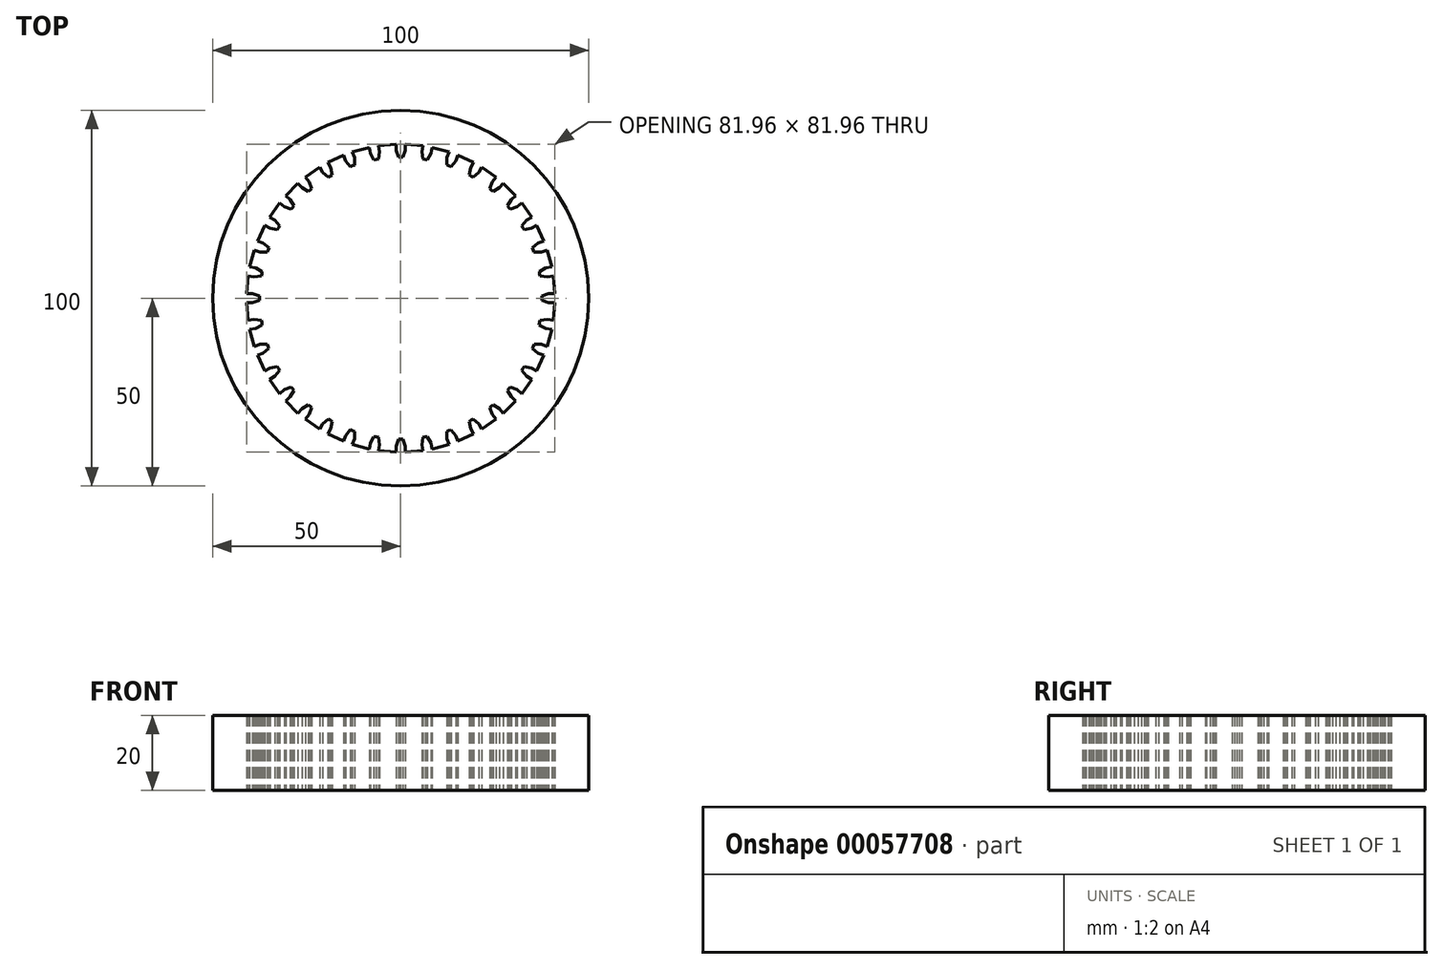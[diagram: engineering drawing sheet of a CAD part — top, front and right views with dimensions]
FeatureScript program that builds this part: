
annotation { "Feature Type Name" : "Feature", "Feature Type Description" : "" }
export const myFeature = defineFeature(function(context is Context, id is Id, definition is map)
    precondition{}
    {
        {
            var Q0;
            Q0=qCreatedBy(makeId("Top.planeOp"),FACE);
            var sketch = newSketch(context, id + "F0", { "sketchPlane" : qUnion([Q0])});
            skCircle(sketch, "E0", {"center": v(0, 0) * mm, "radius": 50 * mm});
            skLineSegment(sketch, "E1", {"start": v(0, 41) * mm, "end": v(0, 37.5) * mm});
            skLineSegment(sketch, "E2.0", {"start": v(-1.25, 40.98) * mm, "end": v(-1.25, 37.78) * mm});
            skLineSegment(sketch, "E3.0", {"start": v(1.25, 40.98) * mm, "end": v(1.25, 37.78) * mm});
            skPoint(sketch, "E4.visualSharp", {"position": v(1.25, 37.48) * mm});
            skPoint(sketch, "E5.visualSharp", {"position": v(-1.25, 37.48) * mm});
            skLineSegment(sketch, "E6.1.0", {"start": v(-8.35, 40.14) * mm, "end": v(-7.8, 36.99) * mm});
            skArc(sketch, "E6.1.1", {"start": v(-7.8, 36.99) * mm, "mid": v(-7.67, 36.8) * mm, "end": v(-7.44, 36.74) * mm});
            skLineSegment(sketch, "E6.1.2", {"start": v(-7.44, 36.74) * mm, "end": v(-5.57, 37.07) * mm});
            skArc(sketch, "E6.1.3", {"start": v(-5.57, 37.07) * mm, "mid": v(-5.38, 37.2) * mm, "end": v(-5.33, 37.42) * mm});
            skLineSegment(sketch, "E6.1.4", {"start": v(-5.89, 40.58) * mm, "end": v(-5.33, 37.42) * mm});
            skLineSegment(sketch, "E6.2.0", {"start": v(-15.2, 38.08) * mm, "end": v(-14.1, 35.07) * mm});
            skArc(sketch, "E6.2.1", {"start": v(-14.1, 35.07) * mm, "mid": v(-13.94, 34.9) * mm, "end": v(-13.71, 34.9) * mm});
            skLineSegment(sketch, "E6.2.2", {"start": v(-13.71, 34.9) * mm, "end": v(-11.93, 35.54) * mm});
            skArc(sketch, "E6.2.3", {"start": v(-11.93, 35.54) * mm, "mid": v(-11.76, 35.7) * mm, "end": v(-11.75, 35.93) * mm});
            skLineSegment(sketch, "E6.2.4", {"start": v(-12.84, 38.94) * mm, "end": v(-11.75, 35.93) * mm});
            skLineSegment(sketch, "E6.3.0", {"start": v(-21.57, 34.87) * mm, "end": v(-19.97, 32.1) * mm});
            skArc(sketch, "E6.3.1", {"start": v(-19.97, 32.1) * mm, "mid": v(-19.79, 31.95) * mm, "end": v(-19.56, 31.98) * mm});
            skLineSegment(sketch, "E6.3.2", {"start": v(-19.56, 31.98) * mm, "end": v(-17.92, 32.93) * mm});
            skArc(sketch, "E6.3.3", {"start": v(-17.92, 32.93) * mm, "mid": v(-17.78, 33.12) * mm, "end": v(-17.8, 33.34) * mm});
            skLineSegment(sketch, "E6.3.4", {"start": v(-19.4, 36.12) * mm, "end": v(-17.8, 33.34) * mm});
            skLineSegment(sketch, "E6.4.0", {"start": v(-27.3, 30.59) * mm, "end": v(-25.24, 28.14) * mm});
            skArc(sketch, "E6.4.1", {"start": v(-25.24, 28.14) * mm, "mid": v(-25.04, 28.03) * mm, "end": v(-24.82, 28.1) * mm});
            skLineSegment(sketch, "E6.4.2", {"start": v(-24.82, 28.1) * mm, "end": v(-23.36, 29.32) * mm});
            skArc(sketch, "E6.4.3", {"start": v(-23.36, 29.32) * mm, "mid": v(-23.26, 29.53) * mm, "end": v(-23.33, 29.74) * mm});
            skLineSegment(sketch, "E6.4.4", {"start": v(-25.38, 32.2) * mm, "end": v(-23.33, 29.74) * mm});
            skLineSegment(sketch, "E6.5.0", {"start": v(-32.2, 25.38) * mm, "end": v(-29.74, 23.33) * mm});
            skArc(sketch, "E6.5.1", {"start": v(-29.74, 23.33) * mm, "mid": v(-29.53, 23.26) * mm, "end": v(-29.32, 23.36) * mm});
            skLineSegment(sketch, "E6.5.2", {"start": v(-29.32, 23.36) * mm, "end": v(-28.1, 24.82) * mm});
            skArc(sketch, "E6.5.3", {"start": v(-28.1, 24.82) * mm, "mid": v(-28.03, 25.04) * mm, "end": v(-28.14, 25.24) * mm});
            skLineSegment(sketch, "E6.5.4", {"start": v(-30.59, 27.3) * mm, "end": v(-28.14, 25.24) * mm});
            skLineSegment(sketch, "E6.6.0", {"start": v(-36.12, 19.4) * mm, "end": v(-33.34, 17.8) * mm});
            skArc(sketch, "E6.6.1", {"start": v(-33.34, 17.8) * mm, "mid": v(-33.12, 17.78) * mm, "end": v(-32.93, 17.92) * mm});
            skLineSegment(sketch, "E6.6.2", {"start": v(-32.93, 17.92) * mm, "end": v(-31.98, 19.56) * mm});
            skArc(sketch, "E6.6.3", {"start": v(-31.98, 19.56) * mm, "mid": v(-31.95, 19.79) * mm, "end": v(-32.1, 19.97) * mm});
            skLineSegment(sketch, "E6.6.4", {"start": v(-34.87, 21.57) * mm, "end": v(-32.1, 19.97) * mm});
            skLineSegment(sketch, "E6.7.0", {"start": v(-38.94, 12.84) * mm, "end": v(-35.93, 11.75) * mm});
            skArc(sketch, "E6.7.1", {"start": v(-35.93, 11.75) * mm, "mid": v(-35.7, 11.76) * mm, "end": v(-35.54, 11.93) * mm});
            skLineSegment(sketch, "E6.7.2", {"start": v(-35.54, 11.93) * mm, "end": v(-34.9, 13.71) * mm});
            skArc(sketch, "E6.7.3", {"start": v(-34.9, 13.71) * mm, "mid": v(-34.9, 13.94) * mm, "end": v(-35.07, 14.1) * mm});
            skLineSegment(sketch, "E6.7.4", {"start": v(-38.08, 15.2) * mm, "end": v(-35.07, 14.1) * mm});
            skLineSegment(sketch, "E6.8.0", {"start": v(-40.58, 5.89) * mm, "end": v(-37.42, 5.33) * mm});
            skArc(sketch, "E6.8.1", {"start": v(-37.42, 5.33) * mm, "mid": v(-37.2, 5.38) * mm, "end": v(-37.07, 5.57) * mm});
            skLineSegment(sketch, "E6.8.2", {"start": v(-37.07, 5.57) * mm, "end": v(-36.74, 7.44) * mm});
            skArc(sketch, "E6.8.3", {"start": v(-36.74, 7.44) * mm, "mid": v(-36.8, 7.67) * mm, "end": v(-36.99, 7.8) * mm});
            skLineSegment(sketch, "E6.8.4", {"start": v(-40.14, 8.35) * mm, "end": v(-36.99, 7.8) * mm});
            skLineSegment(sketch, "E6.9.0", {"start": v(-40.98, -1.25) * mm, "end": v(-37.78, -1.25) * mm});
            skArc(sketch, "E6.9.1", {"start": v(-37.78, -1.25) * mm, "mid": v(-37.57, -1.16) * mm, "end": v(-37.48, -0.95) * mm});
            skLineSegment(sketch, "E6.9.2", {"start": v(-37.48, -0.95) * mm, "end": v(-37.48, 0.95) * mm});
            skArc(sketch, "E6.9.3", {"start": v(-37.48, 0.95) * mm, "mid": v(-37.57, 1.16) * mm, "end": v(-37.78, 1.25) * mm});
            skLineSegment(sketch, "E6.9.4", {"start": v(-40.98, 1.25) * mm, "end": v(-37.78, 1.25) * mm});
            skLineSegment(sketch, "E6.10.0", {"start": v(-40.14, -8.35) * mm, "end": v(-36.99, -7.8) * mm});
            skArc(sketch, "E6.10.1", {"start": v(-36.99, -7.8) * mm, "mid": v(-36.8, -7.67) * mm, "end": v(-36.74, -7.44) * mm});
            skLineSegment(sketch, "E6.10.2", {"start": v(-36.74, -7.44) * mm, "end": v(-37.07, -5.57) * mm});
            skArc(sketch, "E6.10.3", {"start": v(-37.07, -5.57) * mm, "mid": v(-37.2, -5.38) * mm, "end": v(-37.42, -5.33) * mm});
            skLineSegment(sketch, "E6.10.4", {"start": v(-40.58, -5.89) * mm, "end": v(-37.42, -5.33) * mm});
            skLineSegment(sketch, "E6.11.0", {"start": v(-38.08, -15.2) * mm, "end": v(-35.07, -14.1) * mm});
            skArc(sketch, "E6.11.1", {"start": v(-35.07, -14.1) * mm, "mid": v(-34.9, -13.94) * mm, "end": v(-34.9, -13.71) * mm});
            skLineSegment(sketch, "E6.11.2", {"start": v(-34.9, -13.71) * mm, "end": v(-35.54, -11.93) * mm});
            skArc(sketch, "E6.11.3", {"start": v(-35.54, -11.93) * mm, "mid": v(-35.7, -11.76) * mm, "end": v(-35.93, -11.75) * mm});
            skLineSegment(sketch, "E6.11.4", {"start": v(-38.94, -12.84) * mm, "end": v(-35.93, -11.75) * mm});
            skLineSegment(sketch, "E6.12.0", {"start": v(-34.87, -21.57) * mm, "end": v(-32.1, -19.97) * mm});
            skArc(sketch, "E6.12.1", {"start": v(-32.1, -19.97) * mm, "mid": v(-31.95, -19.79) * mm, "end": v(-31.98, -19.56) * mm});
            skLineSegment(sketch, "E6.12.2", {"start": v(-31.98, -19.56) * mm, "end": v(-32.93, -17.92) * mm});
            skArc(sketch, "E6.12.3", {"start": v(-32.93, -17.92) * mm, "mid": v(-33.12, -17.78) * mm, "end": v(-33.34, -17.8) * mm});
            skLineSegment(sketch, "E6.12.4", {"start": v(-36.12, -19.4) * mm, "end": v(-33.34, -17.8) * mm});
            skLineSegment(sketch, "E6.13.0", {"start": v(-30.59, -27.3) * mm, "end": v(-28.14, -25.24) * mm});
            skArc(sketch, "E6.13.1", {"start": v(-28.14, -25.24) * mm, "mid": v(-28.03, -25.04) * mm, "end": v(-28.1, -24.82) * mm});
            skLineSegment(sketch, "E6.13.2", {"start": v(-28.1, -24.82) * mm, "end": v(-29.32, -23.36) * mm});
            skArc(sketch, "E6.13.3", {"start": v(-29.32, -23.36) * mm, "mid": v(-29.53, -23.26) * mm, "end": v(-29.74, -23.33) * mm});
            skLineSegment(sketch, "E6.13.4", {"start": v(-32.2, -25.38) * mm, "end": v(-29.74, -23.33) * mm});
            skLineSegment(sketch, "E6.14.0", {"start": v(-25.38, -32.2) * mm, "end": v(-23.33, -29.74) * mm});
            skArc(sketch, "E6.14.1", {"start": v(-23.33, -29.74) * mm, "mid": v(-23.26, -29.53) * mm, "end": v(-23.36, -29.32) * mm});
            skLineSegment(sketch, "E6.14.2", {"start": v(-23.36, -29.32) * mm, "end": v(-24.82, -28.1) * mm});
            skArc(sketch, "E6.14.3", {"start": v(-24.82, -28.1) * mm, "mid": v(-25.04, -28.03) * mm, "end": v(-25.24, -28.14) * mm});
            skLineSegment(sketch, "E6.14.4", {"start": v(-27.3, -30.59) * mm, "end": v(-25.24, -28.14) * mm});
            skLineSegment(sketch, "E6.15.0", {"start": v(-19.4, -36.12) * mm, "end": v(-17.8, -33.34) * mm});
            skArc(sketch, "E6.15.1", {"start": v(-17.8, -33.34) * mm, "mid": v(-17.78, -33.12) * mm, "end": v(-17.92, -32.93) * mm});
            skLineSegment(sketch, "E6.15.2", {"start": v(-17.92, -32.93) * mm, "end": v(-19.56, -31.98) * mm});
            skArc(sketch, "E6.15.3", {"start": v(-19.56, -31.98) * mm, "mid": v(-19.79, -31.95) * mm, "end": v(-19.97, -32.1) * mm});
            skLineSegment(sketch, "E6.15.4", {"start": v(-21.57, -34.87) * mm, "end": v(-19.97, -32.1) * mm});
            skLineSegment(sketch, "E6.16.0", {"start": v(-12.84, -38.94) * mm, "end": v(-11.75, -35.93) * mm});
            skArc(sketch, "E6.16.1", {"start": v(-11.75, -35.93) * mm, "mid": v(-11.76, -35.7) * mm, "end": v(-11.93, -35.54) * mm});
            skLineSegment(sketch, "E6.16.2", {"start": v(-11.93, -35.54) * mm, "end": v(-13.71, -34.9) * mm});
            skArc(sketch, "E6.16.3", {"start": v(-13.71, -34.9) * mm, "mid": v(-13.94, -34.9) * mm, "end": v(-14.1, -35.07) * mm});
            skLineSegment(sketch, "E6.16.4", {"start": v(-15.2, -38.08) * mm, "end": v(-14.1, -35.07) * mm});
            skLineSegment(sketch, "E6.17.0", {"start": v(-5.89, -40.58) * mm, "end": v(-5.33, -37.42) * mm});
            skArc(sketch, "E6.17.1", {"start": v(-5.33, -37.42) * mm, "mid": v(-5.38, -37.2) * mm, "end": v(-5.57, -37.07) * mm});
            skLineSegment(sketch, "E6.17.2", {"start": v(-5.57, -37.07) * mm, "end": v(-7.44, -36.74) * mm});
            skArc(sketch, "E6.17.3", {"start": v(-7.44, -36.74) * mm, "mid": v(-7.67, -36.8) * mm, "end": v(-7.8, -36.99) * mm});
            skLineSegment(sketch, "E6.17.4", {"start": v(-8.35, -40.14) * mm, "end": v(-7.8, -36.99) * mm});
            skLineSegment(sketch, "E6.18.0", {"start": v(1.25, -40.98) * mm, "end": v(1.25, -37.78) * mm});
            skArc(sketch, "E6.18.1", {"start": v(1.25, -37.78) * mm, "mid": v(1.16, -37.57) * mm, "end": v(0.95, -37.48) * mm});
            skLineSegment(sketch, "E6.18.2", {"start": v(0.95, -37.48) * mm, "end": v(-0.95, -37.48) * mm});
            skArc(sketch, "E6.18.3", {"start": v(-0.95, -37.48) * mm, "mid": v(-1.16, -37.57) * mm, "end": v(-1.25, -37.78) * mm});
            skLineSegment(sketch, "E6.18.4", {"start": v(-1.25, -40.98) * mm, "end": v(-1.25, -37.78) * mm});
            skLineSegment(sketch, "E6.19.0", {"start": v(8.35, -40.14) * mm, "end": v(7.8, -36.99) * mm});
            skArc(sketch, "E6.19.1", {"start": v(7.8, -36.99) * mm, "mid": v(7.67, -36.8) * mm, "end": v(7.44, -36.74) * mm});
            skLineSegment(sketch, "E6.19.2", {"start": v(7.44, -36.74) * mm, "end": v(5.57, -37.07) * mm});
            skArc(sketch, "E6.19.3", {"start": v(5.57, -37.07) * mm, "mid": v(5.38, -37.2) * mm, "end": v(5.33, -37.42) * mm});
            skLineSegment(sketch, "E6.19.4", {"start": v(5.89, -40.58) * mm, "end": v(5.33, -37.42) * mm});
            skLineSegment(sketch, "E6.20.0", {"start": v(15.2, -38.08) * mm, "end": v(14.1, -35.07) * mm});
            skArc(sketch, "E6.20.1", {"start": v(14.1, -35.07) * mm, "mid": v(13.94, -34.9) * mm, "end": v(13.71, -34.9) * mm});
            skLineSegment(sketch, "E6.20.2", {"start": v(13.71, -34.9) * mm, "end": v(11.93, -35.54) * mm});
            skArc(sketch, "E6.20.3", {"start": v(11.93, -35.54) * mm, "mid": v(11.76, -35.7) * mm, "end": v(11.75, -35.93) * mm});
            skLineSegment(sketch, "E6.20.4", {"start": v(12.84, -38.94) * mm, "end": v(11.75, -35.93) * mm});
            skLineSegment(sketch, "E6.21.0", {"start": v(21.57, -34.87) * mm, "end": v(19.97, -32.1) * mm});
            skArc(sketch, "E6.21.1", {"start": v(19.97, -32.1) * mm, "mid": v(19.79, -31.95) * mm, "end": v(19.56, -31.98) * mm});
            skLineSegment(sketch, "E6.21.2", {"start": v(19.56, -31.98) * mm, "end": v(17.92, -32.93) * mm});
            skArc(sketch, "E6.21.3", {"start": v(17.92, -32.93) * mm, "mid": v(17.78, -33.12) * mm, "end": v(17.8, -33.34) * mm});
            skLineSegment(sketch, "E6.21.4", {"start": v(19.4, -36.12) * mm, "end": v(17.8, -33.34) * mm});
            skLineSegment(sketch, "E6.22.0", {"start": v(27.3, -30.59) * mm, "end": v(25.24, -28.14) * mm});
            skArc(sketch, "E6.22.1", {"start": v(25.24, -28.14) * mm, "mid": v(25.04, -28.03) * mm, "end": v(24.82, -28.1) * mm});
            skLineSegment(sketch, "E6.22.2", {"start": v(24.82, -28.1) * mm, "end": v(23.36, -29.32) * mm});
            skArc(sketch, "E6.22.3", {"start": v(23.36, -29.32) * mm, "mid": v(23.26, -29.53) * mm, "end": v(23.33, -29.74) * mm});
            skLineSegment(sketch, "E6.22.4", {"start": v(25.38, -32.2) * mm, "end": v(23.33, -29.74) * mm});
            skLineSegment(sketch, "E6.23.0", {"start": v(32.2, -25.38) * mm, "end": v(29.74, -23.33) * mm});
            skArc(sketch, "E6.23.1", {"start": v(29.74, -23.33) * mm, "mid": v(29.53, -23.26) * mm, "end": v(29.32, -23.36) * mm});
            skLineSegment(sketch, "E6.23.2", {"start": v(29.32, -23.36) * mm, "end": v(28.1, -24.82) * mm});
            skArc(sketch, "E6.23.3", {"start": v(28.1, -24.82) * mm, "mid": v(28.03, -25.04) * mm, "end": v(28.14, -25.24) * mm});
            skLineSegment(sketch, "E6.23.4", {"start": v(30.59, -27.3) * mm, "end": v(28.14, -25.24) * mm});
            skLineSegment(sketch, "E6.24.0", {"start": v(36.12, -19.4) * mm, "end": v(33.34, -17.8) * mm});
            skArc(sketch, "E6.24.1", {"start": v(33.34, -17.8) * mm, "mid": v(33.12, -17.78) * mm, "end": v(32.93, -17.92) * mm});
            skLineSegment(sketch, "E6.24.2", {"start": v(32.93, -17.92) * mm, "end": v(31.98, -19.56) * mm});
            skArc(sketch, "E6.24.3", {"start": v(31.98, -19.56) * mm, "mid": v(31.95, -19.79) * mm, "end": v(32.1, -19.97) * mm});
            skLineSegment(sketch, "E6.24.4", {"start": v(34.87, -21.57) * mm, "end": v(32.1, -19.97) * mm});
            skLineSegment(sketch, "E6.25.0", {"start": v(38.94, -12.84) * mm, "end": v(35.93, -11.75) * mm});
            skArc(sketch, "E6.25.1", {"start": v(35.93, -11.75) * mm, "mid": v(35.7, -11.76) * mm, "end": v(35.54, -11.93) * mm});
            skLineSegment(sketch, "E6.25.2", {"start": v(35.54, -11.93) * mm, "end": v(34.9, -13.71) * mm});
            skArc(sketch, "E6.25.3", {"start": v(34.9, -13.71) * mm, "mid": v(34.9, -13.94) * mm, "end": v(35.07, -14.1) * mm});
            skLineSegment(sketch, "E6.25.4", {"start": v(38.08, -15.2) * mm, "end": v(35.07, -14.1) * mm});
            skLineSegment(sketch, "E6.26.0", {"start": v(40.58, -5.89) * mm, "end": v(37.42, -5.33) * mm});
            skArc(sketch, "E6.26.1", {"start": v(37.42, -5.33) * mm, "mid": v(37.2, -5.38) * mm, "end": v(37.07, -5.57) * mm});
            skLineSegment(sketch, "E6.26.2", {"start": v(37.07, -5.57) * mm, "end": v(36.74, -7.44) * mm});
            skArc(sketch, "E6.26.3", {"start": v(36.74, -7.44) * mm, "mid": v(36.8, -7.67) * mm, "end": v(36.99, -7.8) * mm});
            skLineSegment(sketch, "E6.26.4", {"start": v(40.14, -8.35) * mm, "end": v(36.99, -7.8) * mm});
            skLineSegment(sketch, "E6.27.0", {"start": v(40.98, 1.25) * mm, "end": v(37.78, 1.25) * mm});
            skArc(sketch, "E6.27.1", {"start": v(37.78, 1.25) * mm, "mid": v(37.57, 1.16) * mm, "end": v(37.48, 0.95) * mm});
            skLineSegment(sketch, "E6.27.2", {"start": v(37.48, 0.95) * mm, "end": v(37.48, -0.95) * mm});
            skArc(sketch, "E6.27.3", {"start": v(37.48, -0.95) * mm, "mid": v(37.57, -1.16) * mm, "end": v(37.78, -1.25) * mm});
            skLineSegment(sketch, "E6.27.4", {"start": v(40.98, -1.25) * mm, "end": v(37.78, -1.25) * mm});
            skLineSegment(sketch, "E6.28.0", {"start": v(40.14, 8.35) * mm, "end": v(36.99, 7.8) * mm});
            skArc(sketch, "E6.28.1", {"start": v(36.99, 7.8) * mm, "mid": v(36.8, 7.67) * mm, "end": v(36.74, 7.44) * mm});
            skLineSegment(sketch, "E6.28.2", {"start": v(36.74, 7.44) * mm, "end": v(37.07, 5.57) * mm});
            skArc(sketch, "E6.28.3", {"start": v(37.07, 5.57) * mm, "mid": v(37.2, 5.38) * mm, "end": v(37.42, 5.33) * mm});
            skLineSegment(sketch, "E6.28.4", {"start": v(40.58, 5.89) * mm, "end": v(37.42, 5.33) * mm});
            skLineSegment(sketch, "E6.29.0", {"start": v(38.08, 15.2) * mm, "end": v(35.07, 14.1) * mm});
            skArc(sketch, "E6.29.1", {"start": v(35.07, 14.1) * mm, "mid": v(34.9, 13.94) * mm, "end": v(34.9, 13.71) * mm});
            skLineSegment(sketch, "E6.29.2", {"start": v(34.9, 13.71) * mm, "end": v(35.54, 11.93) * mm});
            skArc(sketch, "E6.29.3", {"start": v(35.54, 11.93) * mm, "mid": v(35.7, 11.76) * mm, "end": v(35.93, 11.75) * mm});
            skLineSegment(sketch, "E6.29.4", {"start": v(38.94, 12.84) * mm, "end": v(35.93, 11.75) * mm});
            skLineSegment(sketch, "E6.30.0", {"start": v(34.87, 21.57) * mm, "end": v(32.1, 19.97) * mm});
            skArc(sketch, "E6.30.1", {"start": v(32.1, 19.97) * mm, "mid": v(31.95, 19.79) * mm, "end": v(31.98, 19.56) * mm});
            skLineSegment(sketch, "E6.30.2", {"start": v(31.98, 19.56) * mm, "end": v(32.93, 17.92) * mm});
            skArc(sketch, "E6.30.3", {"start": v(32.93, 17.92) * mm, "mid": v(33.12, 17.78) * mm, "end": v(33.34, 17.8) * mm});
            skLineSegment(sketch, "E6.30.4", {"start": v(36.12, 19.4) * mm, "end": v(33.34, 17.8) * mm});
            skLineSegment(sketch, "E6.31.0", {"start": v(30.59, 27.3) * mm, "end": v(28.14, 25.24) * mm});
            skArc(sketch, "E6.31.1", {"start": v(28.14, 25.24) * mm, "mid": v(28.03, 25.04) * mm, "end": v(28.1, 24.82) * mm});
            skLineSegment(sketch, "E6.31.2", {"start": v(28.1, 24.82) * mm, "end": v(29.32, 23.36) * mm});
            skArc(sketch, "E6.31.3", {"start": v(29.32, 23.36) * mm, "mid": v(29.53, 23.26) * mm, "end": v(29.74, 23.33) * mm});
            skLineSegment(sketch, "E6.31.4", {"start": v(32.2, 25.38) * mm, "end": v(29.74, 23.33) * mm});
            skLineSegment(sketch, "E6.32.0", {"start": v(25.38, 32.2) * mm, "end": v(23.33, 29.74) * mm});
            skArc(sketch, "E6.32.1", {"start": v(23.33, 29.74) * mm, "mid": v(23.26, 29.53) * mm, "end": v(23.36, 29.32) * mm});
            skLineSegment(sketch, "E6.32.2", {"start": v(23.36, 29.32) * mm, "end": v(24.82, 28.1) * mm});
            skArc(sketch, "E6.32.3", {"start": v(24.82, 28.1) * mm, "mid": v(25.04, 28.03) * mm, "end": v(25.24, 28.14) * mm});
            skLineSegment(sketch, "E6.32.4", {"start": v(27.3, 30.59) * mm, "end": v(25.24, 28.14) * mm});
            skLineSegment(sketch, "E6.33.0", {"start": v(19.4, 36.12) * mm, "end": v(17.8, 33.34) * mm});
            skArc(sketch, "E6.33.1", {"start": v(17.8, 33.34) * mm, "mid": v(17.78, 33.12) * mm, "end": v(17.92, 32.93) * mm});
            skLineSegment(sketch, "E6.33.2", {"start": v(17.92, 32.93) * mm, "end": v(19.56, 31.98) * mm});
            skArc(sketch, "E6.33.3", {"start": v(19.56, 31.98) * mm, "mid": v(19.79, 31.95) * mm, "end": v(19.97, 32.1) * mm});
            skLineSegment(sketch, "E6.33.4", {"start": v(21.57, 34.87) * mm, "end": v(19.97, 32.1) * mm});
            skLineSegment(sketch, "E6.34.0", {"start": v(12.84, 38.94) * mm, "end": v(11.75, 35.93) * mm});
            skArc(sketch, "E6.34.1", {"start": v(11.75, 35.93) * mm, "mid": v(11.76, 35.7) * mm, "end": v(11.93, 35.54) * mm});
            skLineSegment(sketch, "E6.34.2", {"start": v(11.93, 35.54) * mm, "end": v(13.71, 34.9) * mm});
            skArc(sketch, "E6.34.3", {"start": v(13.71, 34.9) * mm, "mid": v(13.94, 34.9) * mm, "end": v(14.1, 35.07) * mm});
            skLineSegment(sketch, "E6.34.4", {"start": v(15.2, 38.08) * mm, "end": v(14.1, 35.07) * mm});
            skLineSegment(sketch, "E6.35.0", {"start": v(5.89, 40.58) * mm, "end": v(5.33, 37.42) * mm});
            skArc(sketch, "E6.35.1", {"start": v(5.33, 37.42) * mm, "mid": v(5.38, 37.2) * mm, "end": v(5.57, 37.07) * mm});
            skLineSegment(sketch, "E6.35.2", {"start": v(5.57, 37.07) * mm, "end": v(7.44, 36.74) * mm});
            skArc(sketch, "E6.35.3", {"start": v(7.44, 36.74) * mm, "mid": v(7.67, 36.8) * mm, "end": v(7.8, 36.99) * mm});
            skLineSegment(sketch, "E6.35.4", {"start": v(8.35, 40.14) * mm, "end": v(7.8, 36.99) * mm});
            skCircle(sketch, "E7", {"center": v(0, 0) * mm, "radius": 37.48 * mm});
            skLineSegment(sketch, "E8", {"start": v(-38.08, 15.2) * mm, "end": v(-36.12, 19.4) * mm});
            skLineSegment(sketch, "E9.1.0", {"start": v(-40.14, 8.35) * mm, "end": v(-38.94, 12.84) * mm});
            skLineSegment(sketch, "E9.2.0", {"start": v(-40.98, 1.25) * mm, "end": v(-40.58, 5.89) * mm});
            skLineSegment(sketch, "E9.3.0", {"start": v(-40.58, -5.89) * mm, "end": v(-40.98, -1.25) * mm});
            skLineSegment(sketch, "E9.4.0", {"start": v(-38.94, -12.84) * mm, "end": v(-40.14, -8.35) * mm});
            skLineSegment(sketch, "E9.5.0", {"start": v(-36.12, -19.4) * mm, "end": v(-38.08, -15.2) * mm});
            skLineSegment(sketch, "E9.6.0", {"start": v(-32.2, -25.38) * mm, "end": v(-34.87, -21.57) * mm});
            skLineSegment(sketch, "E9.7.0", {"start": v(-27.3, -30.59) * mm, "end": v(-30.59, -27.3) * mm});
            skLineSegment(sketch, "E9.8.0", {"start": v(-21.57, -34.87) * mm, "end": v(-25.38, -32.2) * mm});
            skLineSegment(sketch, "E9.9.0", {"start": v(-15.2, -38.08) * mm, "end": v(-19.4, -36.12) * mm});
            skLineSegment(sketch, "E9.10.0", {"start": v(-8.35, -40.14) * mm, "end": v(-12.84, -38.94) * mm});
            skLineSegment(sketch, "E9.11.0", {"start": v(-1.25, -40.98) * mm, "end": v(-5.89, -40.58) * mm});
            skLineSegment(sketch, "E9.12.0", {"start": v(5.89, -40.58) * mm, "end": v(1.25, -40.98) * mm});
            skLineSegment(sketch, "E9.13.0", {"start": v(12.84, -38.94) * mm, "end": v(8.35, -40.14) * mm});
            skLineSegment(sketch, "E9.14.0", {"start": v(19.4, -36.12) * mm, "end": v(15.2, -38.08) * mm});
            skLineSegment(sketch, "E9.15.0", {"start": v(25.38, -32.2) * mm, "end": v(21.57, -34.87) * mm});
            skLineSegment(sketch, "E9.16.0", {"start": v(30.59, -27.3) * mm, "end": v(27.3, -30.59) * mm});
            skLineSegment(sketch, "E9.17.0", {"start": v(34.87, -21.57) * mm, "end": v(32.2, -25.38) * mm});
            skLineSegment(sketch, "E9.18.0", {"start": v(38.08, -15.2) * mm, "end": v(36.12, -19.4) * mm});
            skLineSegment(sketch, "E9.19.0", {"start": v(40.14, -8.35) * mm, "end": v(38.94, -12.84) * mm});
            skLineSegment(sketch, "E9.20.0", {"start": v(40.98, -1.25) * mm, "end": v(40.58, -5.89) * mm});
            skLineSegment(sketch, "E9.21.0", {"start": v(40.58, 5.89) * mm, "end": v(40.98, 1.25) * mm});
            skLineSegment(sketch, "E9.22.0", {"start": v(38.94, 12.84) * mm, "end": v(40.14, 8.35) * mm});
            skLineSegment(sketch, "E9.23.0", {"start": v(36.12, 19.4) * mm, "end": v(38.08, 15.2) * mm});
            skLineSegment(sketch, "E9.24.0", {"start": v(32.2, 25.38) * mm, "end": v(34.87, 21.57) * mm});
            skLineSegment(sketch, "E9.25.0", {"start": v(27.3, 30.59) * mm, "end": v(30.59, 27.3) * mm});
            skLineSegment(sketch, "E9.26.0", {"start": v(21.57, 34.87) * mm, "end": v(25.38, 32.2) * mm});
            skLineSegment(sketch, "E9.27.0", {"start": v(15.2, 38.08) * mm, "end": v(19.4, 36.12) * mm});
            skLineSegment(sketch, "E9.28.0", {"start": v(8.35, 40.14) * mm, "end": v(12.84, 38.94) * mm});
            skLineSegment(sketch, "E9.29.0", {"start": v(1.25, 40.98) * mm, "end": v(5.89, 40.58) * mm});
            skLineSegment(sketch, "E9.30.0", {"start": v(-5.89, 40.58) * mm, "end": v(-1.25, 40.98) * mm});
            skLineSegment(sketch, "E9.31.0", {"start": v(-12.84, 38.94) * mm, "end": v(-8.35, 40.14) * mm});
            skLineSegment(sketch, "E9.32.0", {"start": v(-19.4, 36.12) * mm, "end": v(-15.2, 38.08) * mm});
            skLineSegment(sketch, "E9.33.0", {"start": v(-25.38, 32.2) * mm, "end": v(-21.57, 34.87) * mm});
            skLineSegment(sketch, "E9.34.0", {"start": v(-30.59, 27.3) * mm, "end": v(-27.3, 30.59) * mm});
            skLineSegment(sketch, "E9.35.0", {"start": v(-34.87, 21.57) * mm, "end": v(-32.2, 25.38) * mm});
            skLineSegment(sketch, "E10", {"start": v(0, 37.5) * mm, "end": v(-0.6, 37.52) * mm});
            skLineSegment(sketch, "E11", {"start": v(0, 37.5) * mm, "end": v(0.6, 37.5) * mm});
            skLineSegment(sketch, "E12", {"start": v(-0.6, 37.52) * mm, "end": v(-1.25, 39.38) * mm});
            skLineSegment(sketch, "E13", {"start": v(0.6, 37.5) * mm, "end": v(1.25, 39.38) * mm});
            skLineSegment(sketch, "E14.1.0", {"start": v(-6.51, 36.93) * mm, "end": v(-7.1, 36.85) * mm});
            skLineSegment(sketch, "E14.1.1", {"start": v(-6.51, 36.93) * mm, "end": v(-5.92, 37.03) * mm});
            skLineSegment(sketch, "E14.1.2", {"start": v(-7.1, 36.85) * mm, "end": v(-8.07, 38.56) * mm});
            skLineSegment(sketch, "E14.1.3", {"start": v(-5.92, 37.03) * mm, "end": v(-5.6, 39) * mm});
            skLineSegment(sketch, "E14.2.0", {"start": v(-12.83, 35.24) * mm, "end": v(-13.4, 35.05) * mm});
            skLineSegment(sketch, "E14.2.1", {"start": v(-12.83, 35.24) * mm, "end": v(-12.26, 35.44) * mm});
            skLineSegment(sketch, "E14.2.2", {"start": v(-13.4, 35.05) * mm, "end": v(-14.64, 36.58) * mm});
            skLineSegment(sketch, "E14.2.3", {"start": v(-12.26, 35.44) * mm, "end": v(-12.3, 37.43) * mm});
            skLineSegment(sketch, "E14.3.0", {"start": v(-18.75, 32.48) * mm, "end": v(-19.28, 32.2) * mm});
            skLineSegment(sketch, "E14.3.1", {"start": v(-18.75, 32.48) * mm, "end": v(-18.23, 32.78) * mm});
            skLineSegment(sketch, "E14.3.2", {"start": v(-19.28, 32.2) * mm, "end": v(-20.77, 33.48) * mm});
            skLineSegment(sketch, "E14.3.3", {"start": v(-18.23, 32.78) * mm, "end": v(-18.6, 34.73) * mm});
            skLineSegment(sketch, "E14.4.0", {"start": v(-24.1, 28.73) * mm, "end": v(-24.58, 28.36) * mm});
            skLineSegment(sketch, "E14.4.1", {"start": v(-24.1, 28.73) * mm, "end": v(-23.64, 29.11) * mm});
            skLineSegment(sketch, "E14.4.2", {"start": v(-24.58, 28.36) * mm, "end": v(-26.27, 29.36) * mm});
            skLineSegment(sketch, "E14.4.3", {"start": v(-23.64, 29.11) * mm, "end": v(-24.36, 30.97) * mm});
            skLineSegment(sketch, "E14.5.0", {"start": v(-28.73, 24.1) * mm, "end": v(-29.13, 23.66) * mm});
            skLineSegment(sketch, "E14.5.1", {"start": v(-28.73, 24.1) * mm, "end": v(-28.34, 24.56) * mm});
            skLineSegment(sketch, "E14.5.2", {"start": v(-29.13, 23.66) * mm, "end": v(-30.97, 24.36) * mm});
            skLineSegment(sketch, "E14.5.3", {"start": v(-28.34, 24.56) * mm, "end": v(-29.36, 26.27) * mm});
            skLineSegment(sketch, "E14.6.0", {"start": v(-32.48, 18.75) * mm, "end": v(-32.8, 18.24) * mm});
            skLineSegment(sketch, "E14.6.1", {"start": v(-32.48, 18.75) * mm, "end": v(-32.18, 19.27) * mm});
            skLineSegment(sketch, "E14.6.2", {"start": v(-32.8, 18.24) * mm, "end": v(-34.73, 18.6) * mm});
            skLineSegment(sketch, "E14.6.3", {"start": v(-32.18, 19.27) * mm, "end": v(-33.48, 20.77) * mm});
            skLineSegment(sketch, "E14.7.0", {"start": v(-35.24, 12.83) * mm, "end": v(-35.46, 12.27) * mm});
            skLineSegment(sketch, "E14.7.1", {"start": v(-35.24, 12.83) * mm, "end": v(-35.03, 13.39) * mm});
            skLineSegment(sketch, "E14.7.2", {"start": v(-35.46, 12.27) * mm, "end": v(-37.43, 12.3) * mm});
            skLineSegment(sketch, "E14.7.3", {"start": v(-35.03, 13.39) * mm, "end": v(-36.58, 14.64) * mm});
            skLineSegment(sketch, "E14.8.0", {"start": v(-36.93, 6.51) * mm, "end": v(-37.05, 5.92) * mm});
            skLineSegment(sketch, "E14.8.1", {"start": v(-36.93, 6.51) * mm, "end": v(-36.83, 7.1) * mm});
            skLineSegment(sketch, "E14.8.2", {"start": v(-37.05, 5.92) * mm, "end": v(-39, 5.6) * mm});
            skLineSegment(sketch, "E14.8.3", {"start": v(-36.83, 7.1) * mm, "end": v(-38.56, 8.07) * mm});
            skLineSegment(sketch, "E14.9.0", {"start": v(-37.5, 0) * mm, "end": v(-37.52, -0.6) * mm});
            skLineSegment(sketch, "E14.9.1", {"start": v(-37.5, 0) * mm, "end": v(-37.5, 0.6) * mm});
            skLineSegment(sketch, "E14.9.2", {"start": v(-37.52, -0.6) * mm, "end": v(-39.38, -1.25) * mm});
            skLineSegment(sketch, "E14.9.3", {"start": v(-37.5, 0.6) * mm, "end": v(-39.38, 1.25) * mm});
            skLineSegment(sketch, "E14.10.0", {"start": v(-36.93, -6.51) * mm, "end": v(-36.85, -7.1) * mm});
            skLineSegment(sketch, "E14.10.1", {"start": v(-36.93, -6.51) * mm, "end": v(-37.03, -5.92) * mm});
            skLineSegment(sketch, "E14.10.2", {"start": v(-36.85, -7.1) * mm, "end": v(-38.56, -8.07) * mm});
            skLineSegment(sketch, "E14.10.3", {"start": v(-37.03, -5.92) * mm, "end": v(-39, -5.6) * mm});
            skLineSegment(sketch, "E14.11.0", {"start": v(-35.24, -12.83) * mm, "end": v(-35.05, -13.4) * mm});
            skLineSegment(sketch, "E14.11.1", {"start": v(-35.24, -12.83) * mm, "end": v(-35.44, -12.26) * mm});
            skLineSegment(sketch, "E14.11.2", {"start": v(-35.05, -13.4) * mm, "end": v(-36.58, -14.64) * mm});
            skLineSegment(sketch, "E14.11.3", {"start": v(-35.44, -12.26) * mm, "end": v(-37.43, -12.3) * mm});
            skLineSegment(sketch, "E14.12.0", {"start": v(-32.48, -18.75) * mm, "end": v(-32.2, -19.28) * mm});
            skLineSegment(sketch, "E14.12.1", {"start": v(-32.48, -18.75) * mm, "end": v(-32.78, -18.23) * mm});
            skLineSegment(sketch, "E14.12.2", {"start": v(-32.2, -19.28) * mm, "end": v(-33.48, -20.77) * mm});
            skLineSegment(sketch, "E14.12.3", {"start": v(-32.78, -18.23) * mm, "end": v(-34.73, -18.6) * mm});
            skLineSegment(sketch, "E14.13.0", {"start": v(-28.73, -24.1) * mm, "end": v(-28.36, -24.58) * mm});
            skLineSegment(sketch, "E14.13.1", {"start": v(-28.73, -24.1) * mm, "end": v(-29.11, -23.64) * mm});
            skLineSegment(sketch, "E14.13.2", {"start": v(-28.36, -24.58) * mm, "end": v(-29.36, -26.27) * mm});
            skLineSegment(sketch, "E14.13.3", {"start": v(-29.11, -23.64) * mm, "end": v(-30.97, -24.36) * mm});
            skLineSegment(sketch, "E14.14.0", {"start": v(-24.1, -28.73) * mm, "end": v(-23.66, -29.13) * mm});
            skLineSegment(sketch, "E14.14.1", {"start": v(-24.1, -28.73) * mm, "end": v(-24.56, -28.34) * mm});
            skLineSegment(sketch, "E14.14.2", {"start": v(-23.66, -29.13) * mm, "end": v(-24.36, -30.97) * mm});
            skLineSegment(sketch, "E14.14.3", {"start": v(-24.56, -28.34) * mm, "end": v(-26.27, -29.36) * mm});
            skLineSegment(sketch, "E14.15.0", {"start": v(-18.75, -32.48) * mm, "end": v(-18.24, -32.8) * mm});
            skLineSegment(sketch, "E14.15.1", {"start": v(-18.75, -32.48) * mm, "end": v(-19.27, -32.18) * mm});
            skLineSegment(sketch, "E14.15.2", {"start": v(-18.24, -32.8) * mm, "end": v(-18.6, -34.73) * mm});
            skLineSegment(sketch, "E14.15.3", {"start": v(-19.27, -32.18) * mm, "end": v(-20.77, -33.48) * mm});
            skLineSegment(sketch, "E14.16.0", {"start": v(-12.83, -35.24) * mm, "end": v(-12.27, -35.46) * mm});
            skLineSegment(sketch, "E14.16.1", {"start": v(-12.83, -35.24) * mm, "end": v(-13.39, -35.03) * mm});
            skLineSegment(sketch, "E14.16.2", {"start": v(-12.27, -35.46) * mm, "end": v(-12.3, -37.43) * mm});
            skLineSegment(sketch, "E14.16.3", {"start": v(-13.39, -35.03) * mm, "end": v(-14.64, -36.58) * mm});
            skLineSegment(sketch, "E14.17.0", {"start": v(-6.51, -36.93) * mm, "end": v(-5.92, -37.05) * mm});
            skLineSegment(sketch, "E14.17.1", {"start": v(-6.51, -36.93) * mm, "end": v(-7.1, -36.83) * mm});
            skLineSegment(sketch, "E14.17.2", {"start": v(-5.92, -37.05) * mm, "end": v(-5.6, -39) * mm});
            skLineSegment(sketch, "E14.17.3", {"start": v(-7.1, -36.83) * mm, "end": v(-8.07, -38.56) * mm});
            skLineSegment(sketch, "E14.18.0", {"start": v(0, -37.5) * mm, "end": v(0.6, -37.52) * mm});
            skLineSegment(sketch, "E14.18.1", {"start": v(0, -37.5) * mm, "end": v(-0.6, -37.5) * mm});
            skLineSegment(sketch, "E14.18.2", {"start": v(0.6, -37.52) * mm, "end": v(1.25, -39.38) * mm});
            skLineSegment(sketch, "E14.18.3", {"start": v(-0.6, -37.5) * mm, "end": v(-1.25, -39.38) * mm});
            skLineSegment(sketch, "E14.19.0", {"start": v(6.51, -36.93) * mm, "end": v(7.1, -36.85) * mm});
            skLineSegment(sketch, "E14.19.1", {"start": v(6.51, -36.93) * mm, "end": v(5.92, -37.03) * mm});
            skLineSegment(sketch, "E14.19.2", {"start": v(7.1, -36.85) * mm, "end": v(8.07, -38.56) * mm});
            skLineSegment(sketch, "E14.19.3", {"start": v(5.92, -37.03) * mm, "end": v(5.6, -39) * mm});
            skLineSegment(sketch, "E14.20.0", {"start": v(12.83, -35.24) * mm, "end": v(13.4, -35.05) * mm});
            skLineSegment(sketch, "E14.20.1", {"start": v(12.83, -35.24) * mm, "end": v(12.26, -35.44) * mm});
            skLineSegment(sketch, "E14.20.2", {"start": v(13.4, -35.05) * mm, "end": v(14.64, -36.58) * mm});
            skLineSegment(sketch, "E14.20.3", {"start": v(12.26, -35.44) * mm, "end": v(12.3, -37.43) * mm});
            skLineSegment(sketch, "E14.21.0", {"start": v(18.75, -32.48) * mm, "end": v(19.28, -32.2) * mm});
            skLineSegment(sketch, "E14.21.1", {"start": v(18.75, -32.48) * mm, "end": v(18.23, -32.78) * mm});
            skLineSegment(sketch, "E14.21.2", {"start": v(19.28, -32.2) * mm, "end": v(20.77, -33.48) * mm});
            skLineSegment(sketch, "E14.21.3", {"start": v(18.23, -32.78) * mm, "end": v(18.6, -34.73) * mm});
            skLineSegment(sketch, "E14.22.0", {"start": v(24.1, -28.73) * mm, "end": v(24.58, -28.36) * mm});
            skLineSegment(sketch, "E14.22.1", {"start": v(24.1, -28.73) * mm, "end": v(23.64, -29.11) * mm});
            skLineSegment(sketch, "E14.22.2", {"start": v(24.58, -28.36) * mm, "end": v(26.27, -29.36) * mm});
            skLineSegment(sketch, "E14.22.3", {"start": v(23.64, -29.11) * mm, "end": v(24.36, -30.97) * mm});
            skLineSegment(sketch, "E14.23.0", {"start": v(28.73, -24.1) * mm, "end": v(29.13, -23.66) * mm});
            skLineSegment(sketch, "E14.23.1", {"start": v(28.73, -24.1) * mm, "end": v(28.34, -24.56) * mm});
            skLineSegment(sketch, "E14.23.2", {"start": v(29.13, -23.66) * mm, "end": v(30.97, -24.36) * mm});
            skLineSegment(sketch, "E14.23.3", {"start": v(28.34, -24.56) * mm, "end": v(29.36, -26.27) * mm});
            skLineSegment(sketch, "E14.24.0", {"start": v(32.48, -18.75) * mm, "end": v(32.8, -18.24) * mm});
            skLineSegment(sketch, "E14.24.1", {"start": v(32.48, -18.75) * mm, "end": v(32.18, -19.27) * mm});
            skLineSegment(sketch, "E14.24.2", {"start": v(32.8, -18.24) * mm, "end": v(34.73, -18.6) * mm});
            skLineSegment(sketch, "E14.24.3", {"start": v(32.18, -19.27) * mm, "end": v(33.48, -20.77) * mm});
            skLineSegment(sketch, "E14.25.0", {"start": v(35.24, -12.83) * mm, "end": v(35.46, -12.27) * mm});
            skLineSegment(sketch, "E14.25.1", {"start": v(35.24, -12.83) * mm, "end": v(35.03, -13.39) * mm});
            skLineSegment(sketch, "E14.25.2", {"start": v(35.46, -12.27) * mm, "end": v(37.43, -12.3) * mm});
            skLineSegment(sketch, "E14.25.3", {"start": v(35.03, -13.39) * mm, "end": v(36.58, -14.64) * mm});
            skLineSegment(sketch, "E14.26.0", {"start": v(36.93, -6.51) * mm, "end": v(37.05, -5.92) * mm});
            skLineSegment(sketch, "E14.26.1", {"start": v(36.93, -6.51) * mm, "end": v(36.83, -7.1) * mm});
            skLineSegment(sketch, "E14.26.2", {"start": v(37.05, -5.92) * mm, "end": v(39, -5.6) * mm});
            skLineSegment(sketch, "E14.26.3", {"start": v(36.83, -7.1) * mm, "end": v(38.56, -8.07) * mm});
            skLineSegment(sketch, "E14.27.0", {"start": v(37.5, 0) * mm, "end": v(37.52, 0.6) * mm});
            skLineSegment(sketch, "E14.27.1", {"start": v(37.5, 0) * mm, "end": v(37.5, -0.6) * mm});
            skLineSegment(sketch, "E14.27.2", {"start": v(37.52, 0.6) * mm, "end": v(39.38, 1.25) * mm});
            skLineSegment(sketch, "E14.27.3", {"start": v(37.5, -0.6) * mm, "end": v(39.38, -1.25) * mm});
            skLineSegment(sketch, "E14.28.0", {"start": v(36.93, 6.51) * mm, "end": v(36.85, 7.1) * mm});
            skLineSegment(sketch, "E14.28.1", {"start": v(36.93, 6.51) * mm, "end": v(37.03, 5.92) * mm});
            skLineSegment(sketch, "E14.28.2", {"start": v(36.85, 7.1) * mm, "end": v(38.56, 8.07) * mm});
            skLineSegment(sketch, "E14.28.3", {"start": v(37.03, 5.92) * mm, "end": v(39, 5.6) * mm});
            skLineSegment(sketch, "E14.29.0", {"start": v(35.24, 12.83) * mm, "end": v(35.05, 13.4) * mm});
            skLineSegment(sketch, "E14.29.1", {"start": v(35.24, 12.83) * mm, "end": v(35.44, 12.26) * mm});
            skLineSegment(sketch, "E14.29.2", {"start": v(35.05, 13.4) * mm, "end": v(36.58, 14.64) * mm});
            skLineSegment(sketch, "E14.29.3", {"start": v(35.44, 12.26) * mm, "end": v(37.43, 12.3) * mm});
            skLineSegment(sketch, "E14.30.0", {"start": v(32.48, 18.75) * mm, "end": v(32.2, 19.28) * mm});
            skLineSegment(sketch, "E14.30.1", {"start": v(32.48, 18.75) * mm, "end": v(32.78, 18.23) * mm});
            skLineSegment(sketch, "E14.30.2", {"start": v(32.2, 19.28) * mm, "end": v(33.48, 20.77) * mm});
            skLineSegment(sketch, "E14.30.3", {"start": v(32.78, 18.23) * mm, "end": v(34.73, 18.6) * mm});
            skLineSegment(sketch, "E14.31.0", {"start": v(28.73, 24.1) * mm, "end": v(28.36, 24.58) * mm});
            skLineSegment(sketch, "E14.31.1", {"start": v(28.73, 24.1) * mm, "end": v(29.11, 23.64) * mm});
            skLineSegment(sketch, "E14.31.2", {"start": v(28.36, 24.58) * mm, "end": v(29.36, 26.27) * mm});
            skLineSegment(sketch, "E14.31.3", {"start": v(29.11, 23.64) * mm, "end": v(30.97, 24.36) * mm});
            skLineSegment(sketch, "E14.32.0", {"start": v(24.1, 28.73) * mm, "end": v(23.66, 29.13) * mm});
            skLineSegment(sketch, "E14.32.1", {"start": v(24.1, 28.73) * mm, "end": v(24.56, 28.34) * mm});
            skLineSegment(sketch, "E14.32.2", {"start": v(23.66, 29.13) * mm, "end": v(24.36, 30.97) * mm});
            skLineSegment(sketch, "E14.32.3", {"start": v(24.56, 28.34) * mm, "end": v(26.27, 29.36) * mm});
            skLineSegment(sketch, "E14.33.0", {"start": v(18.75, 32.48) * mm, "end": v(18.24, 32.8) * mm});
            skLineSegment(sketch, "E14.33.1", {"start": v(18.75, 32.48) * mm, "end": v(19.27, 32.18) * mm});
            skLineSegment(sketch, "E14.33.2", {"start": v(18.24, 32.8) * mm, "end": v(18.6, 34.73) * mm});
            skLineSegment(sketch, "E14.33.3", {"start": v(19.27, 32.18) * mm, "end": v(20.77, 33.48) * mm});
            skLineSegment(sketch, "E14.34.0", {"start": v(12.83, 35.24) * mm, "end": v(12.27, 35.46) * mm});
            skLineSegment(sketch, "E14.34.1", {"start": v(12.83, 35.24) * mm, "end": v(13.39, 35.03) * mm});
            skLineSegment(sketch, "E14.34.2", {"start": v(12.27, 35.46) * mm, "end": v(12.3, 37.43) * mm});
            skLineSegment(sketch, "E14.34.3", {"start": v(13.39, 35.03) * mm, "end": v(14.64, 36.58) * mm});
            skLineSegment(sketch, "E14.35.0", {"start": v(6.51, 36.93) * mm, "end": v(5.92, 37.05) * mm});
            skLineSegment(sketch, "E14.35.1", {"start": v(6.51, 36.93) * mm, "end": v(7.1, 36.83) * mm});
            skLineSegment(sketch, "E14.35.2", {"start": v(5.92, 37.05) * mm, "end": v(5.6, 39) * mm});
            skLineSegment(sketch, "E14.35.3", {"start": v(7.1, 36.83) * mm, "end": v(8.07, 38.56) * mm});
            skSolve(sketch);
        }
        {
            var Q0;
            Q0=makeQuery(id+"F0.imprint","IMPRINT",FACE,{"disambiguationData":[TD([[makeQuery(id+"F0.imprint","IMPRINT",EDGE,{"derivedFrom":sQuery(id+"F0.wireOp",EDGE,"E0")}),1.0]])]});
            extrude(context, id + "F1", {"entities" : qUnion([Q0]), "depth" : 20 * mm});
        }
    });
